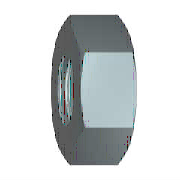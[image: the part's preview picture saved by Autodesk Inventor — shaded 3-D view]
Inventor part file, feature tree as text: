
AUTODESK INVENTOR PART (.ipt)
format: ipt  version: 2022 (Build 260153000, 153)  size: 172,544 bytes
history: native  units: mm (DEFAULTED — no unit token found)
features: sketch x3, other x2, extrude x1, hole x1, plane x1
ambient origin geometry x7: Origin, YZ Plane, XZ Plane, X Axis, Y Axis, Z Axis, Center Point
bodies: Solid1 (feature_tree)
feature tree (8):
  extrude  "Базовый элемент"  Depth=9.237604mm
  other  "Фаска1"
  hole  "Резьба"  [1 undecoded]
  other  "Work Axis1"
  plane  "Work Plane1"
  sketch  "Эскиз1"
  sketch  "Эскиз2"
  sketch  "Эскиз3"
note: 1 required parameter value undecoded (feature->parameter linkage not recoverable at this tier; creation-order binding heuristic only, values carry confidence <= 0.55)
